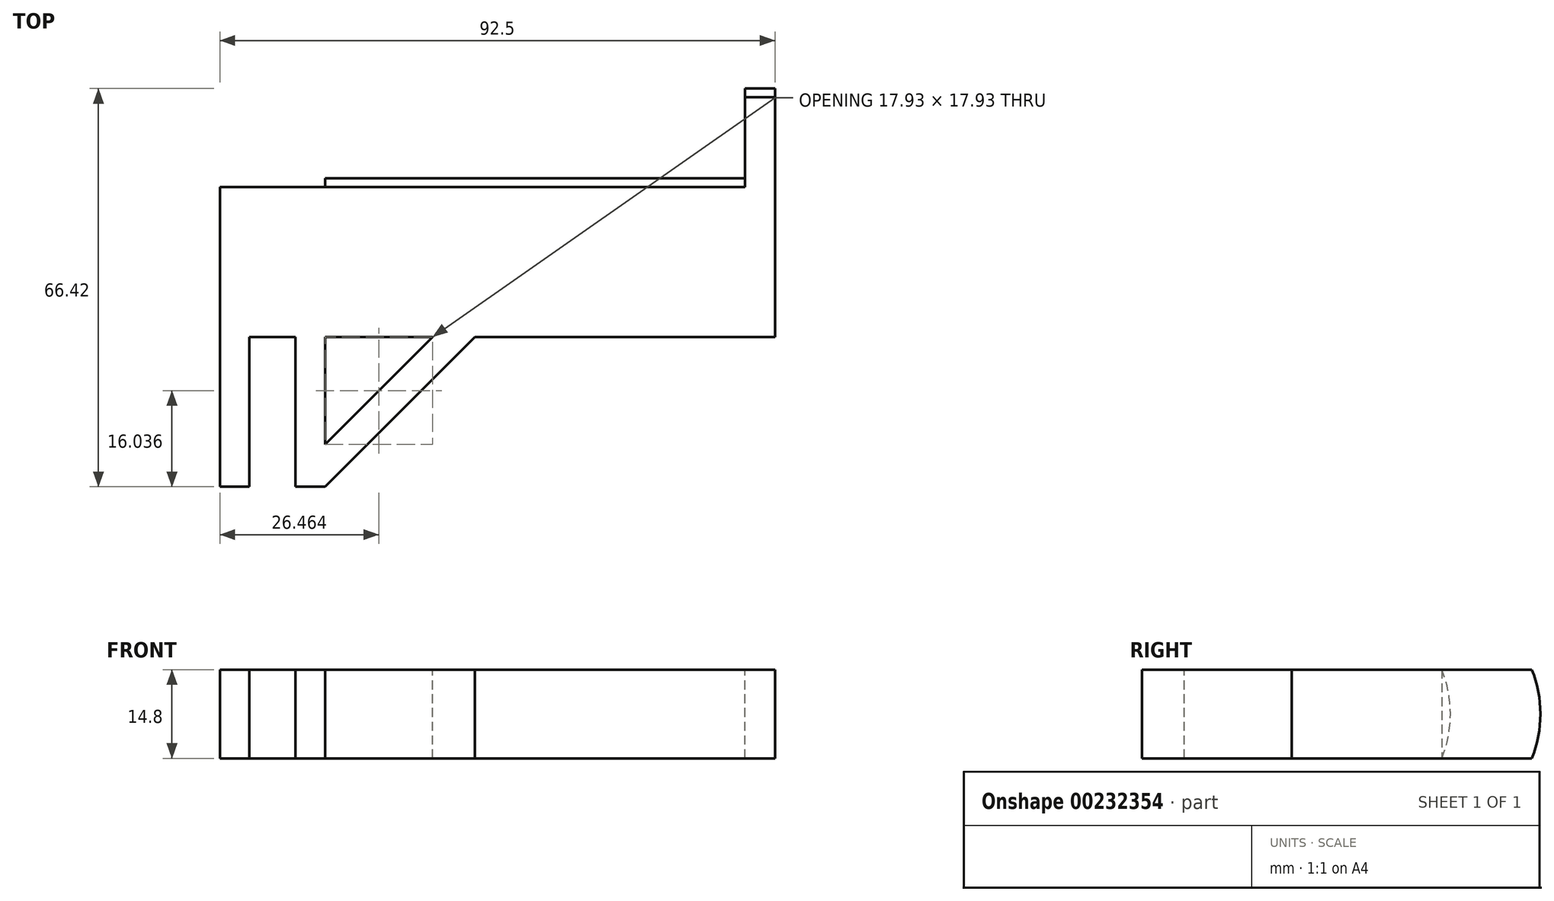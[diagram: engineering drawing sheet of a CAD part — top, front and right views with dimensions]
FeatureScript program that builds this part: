
annotation { "Feature Type Name" : "Feature", "Feature Type Description" : "" }
export const myFeature = defineFeature(function(context is Context, id is Id, definition is map)
    precondition{}
    {
        {
            var Q0;
            Q0=qCreatedBy(makeId("Top.planeOp"),FACE);
            var sketch = newSketch(context, id + "F0", { "sketchPlane" : qUnion([Q0])});
            skLineSegment(sketch, "E0.bottom", {"start": v(0, 0) * mm, "end": v(4.9, 0) * mm});
            skLineSegment(sketch, "E0.top", {"start": v(0, 50) * mm, "end": v(17.5, 50) * mm});
            skLineSegment(sketch, "E0.left", {"start": v(0, 0) * mm, "end": v(0, 50) * mm});
            skLineSegment(sketch, "E0.right", {"start": v(17.5, 0) * mm, "end": v(17.5, 50) * mm});
            skLineSegment(sketch, "E1.top", {"start": v(4.9, 25) * mm, "end": v(12.6, 25) * mm});
            skLineSegment(sketch, "E1.left", {"start": v(4.9, 0) * mm, "end": v(4.9, 25) * mm});
            skLineSegment(sketch, "E1.right", {"start": v(12.6, 0) * mm, "end": v(12.6, 25) * mm});
            skLineSegment(sketch, "E2.trimOffspring", {"start": v(12.6, 0) * mm, "end": v(17.5, 0) * mm});
            skSolve(sketch);
        }
        {
            var Q0;
            Q0 = qSketchRegion(id + "F0", true);
            extrude(context, id + "F1", {"entities" : qUnion([Q0]), "depth" : 14.8 * mm});
        }
        {
            var Q0;
            Q0=makeQuery(id+"F1.opExtrude","SWEPT_FACE",FACE,{"disambiguationData":[OSD([sQuery(id+"F0.wireOp",EDGE,"E0.right")])]});
            var sketch = newSketch(context, id + "F2", { "sketchPlane" : qUnion([Q0])});
            skLineSegment(sketch, "E3.bottom", {"start": v(50, 14.8) * mm, "end": v(25, 14.8) * mm});
            skLineSegment(sketch, "E3.top", {"start": v(50, 0) * mm, "end": v(25, 0) * mm});
            skLineSegment(sketch, "E3.right", {"start": v(25, 14.8) * mm, "end": v(25, 0) * mm});
            skArc(sketch, "E4", {"start": v(50, 0) * mm, "mid": v(51.42, 7.4) * mm, "end": v(50, 14.8) * mm});
            skSolve(sketch);
        }
        {
            var Q0;
            Q0 = qSketchRegion(id + "F2", true);
            extrude(context, id + "F3", {"entities" : qUnion([Q0]), "operationType" : NewBodyOperationType.ADD, "depth" : 70 * mm});
        }
        {
            var Q0;
            Q0=makeQuery(id+"F3.opExtrude","CAP_FACE",FACE,{"disambiguationData":[OSD([sQuery(id+"F2.wireOp",EDGE,"E3.bottom"),sQuery(id+"F2.wireOp",EDGE,"E3.top"),sQuery(id+"F2.wireOp",EDGE,"E3.right"),sQuery(id+"F2.wireOp",EDGE,"E4")])],"isStart":false});
            var sketch = newSketch(context, id + "F4", { "sketchPlane" : qUnion([Q0])});
            skLineSegment(sketch, "E5.bottom", {"start": v(25, 14.8) * mm, "end": v(65, 14.8) * mm});
            skLineSegment(sketch, "E5.top", {"start": v(25, 0) * mm, "end": v(65, 0) * mm});
            skLineSegment(sketch, "E5.left", {"start": v(25, 14.8) * mm, "end": v(25, 0) * mm});
            skArc(sketch, "E6", {"start": v(65, 0) * mm, "mid": v(66.42, 7.4) * mm, "end": v(65, 14.8) * mm});
            skSolve(sketch);
        }
        {
            var Q0;
            Q0 = qSketchRegion(id + "F4", true);
            extrude(context, id + "F5", {"entities" : qUnion([Q0]), "operationType" : NewBodyOperationType.ADD, "depth" : 5 * mm});
        }
        {
            var Q0;
            Q0=makeQuery(id+"F5.boolean.opBoolean","MERGE",FACE,{"derivedFrom":[makeQuery(id+"F3.boolean.opBoolean","MERGE",FACE,{"derivedFrom":[makeQuery(id+"F1.opExtrude","CAP_FACE",FACE,{"disambiguationData":[OSD([sQuery(id+"F0.wireOp",EDGE,"E0.bottom"),sQuery(id+"F0.wireOp",EDGE,"E0.top"),sQuery(id+"F0.wireOp",EDGE,"E0.left"),sQuery(id+"F0.wireOp",EDGE,"E0.right"),sQuery(id+"F0.wireOp",EDGE,"E1.top"),sQuery(id+"F0.wireOp",EDGE,"E1.left"),sQuery(id+"F0.wireOp",EDGE,"E1.right"),sQuery(id+"F0.wireOp",EDGE,"E2.trimOffspring")])],"isStart":false}),makeQuery(id+"F3.opExtrude","SWEPT_FACE",FACE,{"disambiguationData":[OSD([sQuery(id+"F2.wireOp",EDGE,"E3.bottom")])]})]}),makeQuery(id+"F5.opExtrude","SWEPT_FACE",FACE,{"disambiguationData":[OSD([sQuery(id+"F4.wireOp",EDGE,"E5.bottom")])]})]});
            var sketch = newSketch(context, id + "F6", { "sketchPlane" : qUnion([Q0])});
            skLineSegment(sketch, "E7", {"start": v(17.5, 0) * mm, "end": v(42.5, 25) * mm});
            skLineSegment(sketch, "E8", {"start": v(42.5, 25) * mm, "end": v(35.43, 25) * mm});
            skLineSegment(sketch, "E9", {"start": v(35.43, 25) * mm, "end": v(17.5, 7.07) * mm});
            skLineSegment(sketch, "E10", {"start": v(17.5, 7.07) * mm, "end": v(17.5, 0) * mm});
            skSolve(sketch);
        }
        {
            var Q0;
            Q0 = qSketchRegion(id + "F6", true);
            var Q1;
            Q1=makeQuery(id+"F5.boolean.opBoolean","MERGE",FACE,{"derivedFrom":[makeQuery(id+"F3.boolean.opBoolean","MERGE",FACE,{"derivedFrom":[makeQuery(id+"F1.opExtrude","CAP_FACE",FACE,{"disambiguationData":[OSD([sQuery(id+"F0.wireOp",EDGE,"E0.bottom"),sQuery(id+"F0.wireOp",EDGE,"E0.top"),sQuery(id+"F0.wireOp",EDGE,"E0.left"),sQuery(id+"F0.wireOp",EDGE,"E0.right"),sQuery(id+"F0.wireOp",EDGE,"E1.top"),sQuery(id+"F0.wireOp",EDGE,"E1.left"),sQuery(id+"F0.wireOp",EDGE,"E1.right"),sQuery(id+"F0.wireOp",EDGE,"E2.trimOffspring")])],"isStart":true}),makeQuery(id+"F3.opExtrude","SWEPT_FACE",FACE,{"disambiguationData":[OSD([sQuery(id+"F2.wireOp",EDGE,"E3.top")])]})]}),makeQuery(id+"F5.opExtrude","SWEPT_FACE",FACE,{"disambiguationData":[OSD([sQuery(id+"F4.wireOp",EDGE,"E5.top")])]})]});
            extrude(context, id + "F7", {"entities" : qUnion([Q0]), "operationType" : NewBodyOperationType.ADD, "endBound" : BoundingType.UP_TO_SURFACE, "oppositeDirection" : true, "endBoundEntityFace" : qUnion([Q1]), "depth" : 25 * mm});
        }
    });
